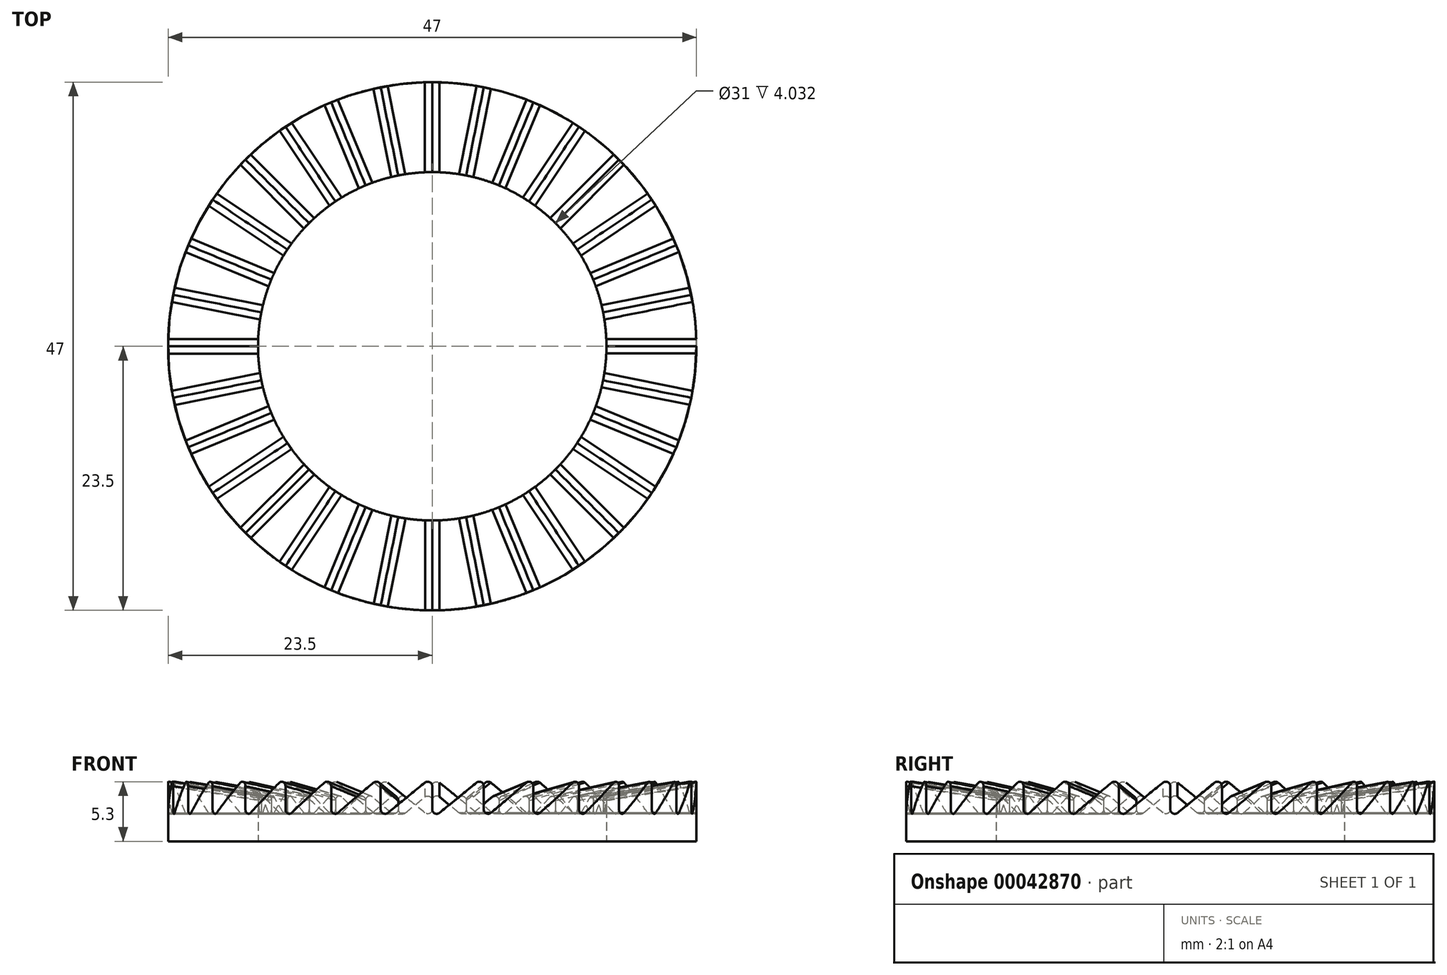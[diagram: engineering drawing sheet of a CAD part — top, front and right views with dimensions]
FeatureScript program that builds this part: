
annotation { "Feature Type Name" : "Feature", "Feature Type Description" : "" }
export const myFeature = defineFeature(function(context is Context, id is Id, definition is map)
    precondition{}
    {
        {
            var Q0;
            Q0=qCreatedBy(makeId("Top.planeOp"),FACE);
            var sketch = newSketch(context, id + "F0", { "sketchPlane" : qUnion([Q0])});
            skCircle(sketch, "E0", {"center": v(0, 0) * mm, "radius": 24 * mm});
            skCircle(sketch, "E1", {"center": v(0, 0) * mm, "radius": 25 * mm});
            skCircle(sketch, "E2", {"center": v(0, 0) * mm, "radius": 13 * mm});
            skCircle(sketch, "E3", {"center": v(0, 0) * mm, "radius": 15.5 * mm});
            skCircle(sketch, "E4", {"center": v(0, 0) * mm, "radius": 23.5 * mm});
            skCircle(sketch, "E5", {"center": v(0, 0) * mm, "radius": 12.5 * mm});
            skSolve(sketch);
        }
        {
            var Q0;
            Q0=makeQuery(id+"F0.imprint","IMPRINT",FACE,{"disambiguationData":[TD([[makeQuery(id+"F0.imprint","IMPRINT",EDGE,{"derivedFrom":sQuery(id+"F0.wireOp",EDGE,"E3")}),-1.0]])]});
            extrude(context, id + "F1", {"entities" : qUnion([Q0]), "depth" : 10 * mm});
        }
        {
            var Q0;
            Q0=qCreatedBy(makeId("Right.planeOp"),FACE);
            var sketch = newSketch(context, id + "F2", { "sketchPlane" : qUnion([Q0])});
            skLineSegment(sketch, "E6", {"start": v(0, 10) * mm, "end": v(0, 2) * mm});
            skLineSegment(sketch, "E7", {"start": v(0, 2) * mm, "end": v(9.8, 10) * mm});
            skLineSegment(sketch, "E8", {"start": v(0, 10) * mm, "end": v(9.8, 10) * mm});
            skSolve(sketch);
        }
        {
            var Q0;
            Q0=makeQuery(id+"F2.imprint","IMPRINT",FACE,{"disambiguationData":[TD([[makeQuery(id+"F2.imprint","IMPRINT",EDGE,{"derivedFrom":sQuery(id+"F2.wireOp",EDGE,"E6")}),1.0]])]});
            extrude(context, id + "F3", {"entities" : qUnion([Q0]), "depth" : 23.5 * mm});
        }
        {
            var Q0;
            Q0=makeQuery(id+"F3.opExtrude","SWEPT_BODY",BODY,{"disambiguationData":[OSD([sQuery(id+"F2.wireOp",EDGE,"E6"),sQuery(id+"F2.wireOp",EDGE,"E7"),sQuery(id+"F2.wireOp",EDGE,"E8")])]});
            var Q1;
            Q1=makeQuery(id+"F3.opExtrude","CAP_EDGE",EDGE,{"disambiguationData":[OSD([sQuery(id+"F2.wireOp",EDGE,"E6")])],"isStart":true});
            circularPattern(context, id + "F4", {"entities" : qUnion([Q0]), "axis" : qUnion([Q1]), "angle" : 11.25 * degree, "instanceCount" : 32});
        }
        {
            var Q0;
            Q0=makeQuery(id+"F3.opExtrude","SWEPT_BODY",BODY,{"disambiguationData":[OSD([sQuery(id+"F2.wireOp",EDGE,"E6"),sQuery(id+"F2.wireOp",EDGE,"E7"),sQuery(id+"F2.wireOp",EDGE,"E8")])]});
            var Q1;
            Q1=makeQuery(id+"F4.opPattern","COPY",BODY,{"derivedFrom":makeQuery(id+"F3.opExtrude","SWEPT_BODY",BODY,{"disambiguationData":[OSD([sQuery(id+"F2.wireOp",EDGE,"E6"),sQuery(id+"F2.wireOp",EDGE,"E7"),sQuery(id+"F2.wireOp",EDGE,"E8")])]}),"instanceName":"1"});
            var Q2;
            Q2=makeQuery(id+"F4.opPattern","COPY",BODY,{"derivedFrom":makeQuery(id+"F3.opExtrude","SWEPT_BODY",BODY,{"disambiguationData":[OSD([sQuery(id+"F2.wireOp",EDGE,"E6"),sQuery(id+"F2.wireOp",EDGE,"E7"),sQuery(id+"F2.wireOp",EDGE,"E8")])]}),"instanceName":"2"});
            var Q3;
            Q3=makeQuery(id+"F4.opPattern","COPY",BODY,{"derivedFrom":makeQuery(id+"F3.opExtrude","SWEPT_BODY",BODY,{"disambiguationData":[OSD([sQuery(id+"F2.wireOp",EDGE,"E6"),sQuery(id+"F2.wireOp",EDGE,"E7"),sQuery(id+"F2.wireOp",EDGE,"E8")])]}),"instanceName":"3"});
            var Q4;
            Q4=makeQuery(id+"F4.opPattern","COPY",BODY,{"derivedFrom":makeQuery(id+"F3.opExtrude","SWEPT_BODY",BODY,{"disambiguationData":[OSD([sQuery(id+"F2.wireOp",EDGE,"E6"),sQuery(id+"F2.wireOp",EDGE,"E7"),sQuery(id+"F2.wireOp",EDGE,"E8")])]}),"instanceName":"4"});
            var Q5;
            Q5=makeQuery(id+"F4.opPattern","COPY",BODY,{"derivedFrom":makeQuery(id+"F3.opExtrude","SWEPT_BODY",BODY,{"disambiguationData":[OSD([sQuery(id+"F2.wireOp",EDGE,"E6"),sQuery(id+"F2.wireOp",EDGE,"E7"),sQuery(id+"F2.wireOp",EDGE,"E8")])]}),"instanceName":"5"});
            var Q6;
            Q6=makeQuery(id+"F4.opPattern","COPY",BODY,{"derivedFrom":makeQuery(id+"F3.opExtrude","SWEPT_BODY",BODY,{"disambiguationData":[OSD([sQuery(id+"F2.wireOp",EDGE,"E6"),sQuery(id+"F2.wireOp",EDGE,"E7"),sQuery(id+"F2.wireOp",EDGE,"E8")])]}),"instanceName":"6"});
            var Q7;
            Q7=makeQuery(id+"F4.opPattern","COPY",BODY,{"derivedFrom":makeQuery(id+"F3.opExtrude","SWEPT_BODY",BODY,{"disambiguationData":[OSD([sQuery(id+"F2.wireOp",EDGE,"E6"),sQuery(id+"F2.wireOp",EDGE,"E7"),sQuery(id+"F2.wireOp",EDGE,"E8")])]}),"instanceName":"7"});
            var Q8;
            Q8=makeQuery(id+"F4.opPattern","COPY",BODY,{"derivedFrom":makeQuery(id+"F3.opExtrude","SWEPT_BODY",BODY,{"disambiguationData":[OSD([sQuery(id+"F2.wireOp",EDGE,"E6"),sQuery(id+"F2.wireOp",EDGE,"E7"),sQuery(id+"F2.wireOp",EDGE,"E8")])]}),"instanceName":"8"});
            var Q9;
            Q9=makeQuery(id+"F4.opPattern","COPY",BODY,{"derivedFrom":makeQuery(id+"F3.opExtrude","SWEPT_BODY",BODY,{"disambiguationData":[OSD([sQuery(id+"F2.wireOp",EDGE,"E6"),sQuery(id+"F2.wireOp",EDGE,"E7"),sQuery(id+"F2.wireOp",EDGE,"E8")])]}),"instanceName":"9"});
            var Q10;
            Q10=makeQuery(id+"F4.opPattern","COPY",BODY,{"derivedFrom":makeQuery(id+"F3.opExtrude","SWEPT_BODY",BODY,{"disambiguationData":[OSD([sQuery(id+"F2.wireOp",EDGE,"E6"),sQuery(id+"F2.wireOp",EDGE,"E7"),sQuery(id+"F2.wireOp",EDGE,"E8")])]}),"instanceName":"10"});
            var Q11;
            Q11=makeQuery(id+"F4.opPattern","COPY",BODY,{"derivedFrom":makeQuery(id+"F3.opExtrude","SWEPT_BODY",BODY,{"disambiguationData":[OSD([sQuery(id+"F2.wireOp",EDGE,"E6"),sQuery(id+"F2.wireOp",EDGE,"E7"),sQuery(id+"F2.wireOp",EDGE,"E8")])]}),"instanceName":"11"});
            var Q12;
            Q12=makeQuery(id+"F4.opPattern","COPY",BODY,{"derivedFrom":makeQuery(id+"F3.opExtrude","SWEPT_BODY",BODY,{"disambiguationData":[OSD([sQuery(id+"F2.wireOp",EDGE,"E6"),sQuery(id+"F2.wireOp",EDGE,"E7"),sQuery(id+"F2.wireOp",EDGE,"E8")])]}),"instanceName":"12"});
            var Q13;
            Q13=makeQuery(id+"F4.opPattern","COPY",BODY,{"derivedFrom":makeQuery(id+"F3.opExtrude","SWEPT_BODY",BODY,{"disambiguationData":[OSD([sQuery(id+"F2.wireOp",EDGE,"E6"),sQuery(id+"F2.wireOp",EDGE,"E7"),sQuery(id+"F2.wireOp",EDGE,"E8")])]}),"instanceName":"13"});
            var Q14;
            Q14=makeQuery(id+"F4.opPattern","COPY",BODY,{"derivedFrom":makeQuery(id+"F3.opExtrude","SWEPT_BODY",BODY,{"disambiguationData":[OSD([sQuery(id+"F2.wireOp",EDGE,"E6"),sQuery(id+"F2.wireOp",EDGE,"E7"),sQuery(id+"F2.wireOp",EDGE,"E8")])]}),"instanceName":"14"});
            var Q15;
            Q15=makeQuery(id+"F4.opPattern","COPY",BODY,{"derivedFrom":makeQuery(id+"F3.opExtrude","SWEPT_BODY",BODY,{"disambiguationData":[OSD([sQuery(id+"F2.wireOp",EDGE,"E6"),sQuery(id+"F2.wireOp",EDGE,"E7"),sQuery(id+"F2.wireOp",EDGE,"E8")])]}),"instanceName":"15"});
            var Q16;
            Q16=makeQuery(id+"F4.opPattern","COPY",BODY,{"derivedFrom":makeQuery(id+"F3.opExtrude","SWEPT_BODY",BODY,{"disambiguationData":[OSD([sQuery(id+"F2.wireOp",EDGE,"E6"),sQuery(id+"F2.wireOp",EDGE,"E7"),sQuery(id+"F2.wireOp",EDGE,"E8")])]}),"instanceName":"16"});
            var Q17;
            Q17=makeQuery(id+"F4.opPattern","COPY",BODY,{"derivedFrom":makeQuery(id+"F3.opExtrude","SWEPT_BODY",BODY,{"disambiguationData":[OSD([sQuery(id+"F2.wireOp",EDGE,"E6"),sQuery(id+"F2.wireOp",EDGE,"E7"),sQuery(id+"F2.wireOp",EDGE,"E8")])]}),"instanceName":"17"});
            var Q18;
            Q18=makeQuery(id+"F4.opPattern","COPY",BODY,{"derivedFrom":makeQuery(id+"F3.opExtrude","SWEPT_BODY",BODY,{"disambiguationData":[OSD([sQuery(id+"F2.wireOp",EDGE,"E6"),sQuery(id+"F2.wireOp",EDGE,"E7"),sQuery(id+"F2.wireOp",EDGE,"E8")])]}),"instanceName":"18"});
            var Q19;
            Q19=makeQuery(id+"F4.opPattern","COPY",BODY,{"derivedFrom":makeQuery(id+"F3.opExtrude","SWEPT_BODY",BODY,{"disambiguationData":[OSD([sQuery(id+"F2.wireOp",EDGE,"E6"),sQuery(id+"F2.wireOp",EDGE,"E7"),sQuery(id+"F2.wireOp",EDGE,"E8")])]}),"instanceName":"19"});
            var Q20;
            Q20=makeQuery(id+"F4.opPattern","COPY",BODY,{"derivedFrom":makeQuery(id+"F3.opExtrude","SWEPT_BODY",BODY,{"disambiguationData":[OSD([sQuery(id+"F2.wireOp",EDGE,"E6"),sQuery(id+"F2.wireOp",EDGE,"E7"),sQuery(id+"F2.wireOp",EDGE,"E8")])]}),"instanceName":"20"});
            var Q21;
            Q21=makeQuery(id+"F4.opPattern","COPY",BODY,{"derivedFrom":makeQuery(id+"F3.opExtrude","SWEPT_BODY",BODY,{"disambiguationData":[OSD([sQuery(id+"F2.wireOp",EDGE,"E6"),sQuery(id+"F2.wireOp",EDGE,"E7"),sQuery(id+"F2.wireOp",EDGE,"E8")])]}),"instanceName":"21"});
            var Q22;
            Q22=makeQuery(id+"F4.opPattern","COPY",BODY,{"derivedFrom":makeQuery(id+"F3.opExtrude","SWEPT_BODY",BODY,{"disambiguationData":[OSD([sQuery(id+"F2.wireOp",EDGE,"E6"),sQuery(id+"F2.wireOp",EDGE,"E7"),sQuery(id+"F2.wireOp",EDGE,"E8")])]}),"instanceName":"22"});
            var Q23;
            Q23=makeQuery(id+"F4.opPattern","COPY",BODY,{"derivedFrom":makeQuery(id+"F3.opExtrude","SWEPT_BODY",BODY,{"disambiguationData":[OSD([sQuery(id+"F2.wireOp",EDGE,"E6"),sQuery(id+"F2.wireOp",EDGE,"E7"),sQuery(id+"F2.wireOp",EDGE,"E8")])]}),"instanceName":"23"});
            var Q24;
            Q24=makeQuery(id+"F4.opPattern","COPY",BODY,{"derivedFrom":makeQuery(id+"F3.opExtrude","SWEPT_BODY",BODY,{"disambiguationData":[OSD([sQuery(id+"F2.wireOp",EDGE,"E6"),sQuery(id+"F2.wireOp",EDGE,"E7"),sQuery(id+"F2.wireOp",EDGE,"E8")])]}),"instanceName":"24"});
            var Q25;
            Q25=makeQuery(id+"F4.opPattern","COPY",BODY,{"derivedFrom":makeQuery(id+"F3.opExtrude","SWEPT_BODY",BODY,{"disambiguationData":[OSD([sQuery(id+"F2.wireOp",EDGE,"E6"),sQuery(id+"F2.wireOp",EDGE,"E7"),sQuery(id+"F2.wireOp",EDGE,"E8")])]}),"instanceName":"25"});
            var Q26;
            Q26=makeQuery(id+"F4.opPattern","COPY",BODY,{"derivedFrom":makeQuery(id+"F3.opExtrude","SWEPT_BODY",BODY,{"disambiguationData":[OSD([sQuery(id+"F2.wireOp",EDGE,"E6"),sQuery(id+"F2.wireOp",EDGE,"E7"),sQuery(id+"F2.wireOp",EDGE,"E8")])]}),"instanceName":"26"});
            var Q27;
            Q27=makeQuery(id+"F4.opPattern","COPY",BODY,{"derivedFrom":makeQuery(id+"F3.opExtrude","SWEPT_BODY",BODY,{"disambiguationData":[OSD([sQuery(id+"F2.wireOp",EDGE,"E6"),sQuery(id+"F2.wireOp",EDGE,"E7"),sQuery(id+"F2.wireOp",EDGE,"E8")])]}),"instanceName":"27"});
            var Q28;
            Q28=makeQuery(id+"F4.opPattern","COPY",BODY,{"derivedFrom":makeQuery(id+"F3.opExtrude","SWEPT_BODY",BODY,{"disambiguationData":[OSD([sQuery(id+"F2.wireOp",EDGE,"E6"),sQuery(id+"F2.wireOp",EDGE,"E7"),sQuery(id+"F2.wireOp",EDGE,"E8")])]}),"instanceName":"28"});
            var Q29;
            Q29=makeQuery(id+"F4.opPattern","COPY",BODY,{"derivedFrom":makeQuery(id+"F3.opExtrude","SWEPT_BODY",BODY,{"disambiguationData":[OSD([sQuery(id+"F2.wireOp",EDGE,"E6"),sQuery(id+"F2.wireOp",EDGE,"E7"),sQuery(id+"F2.wireOp",EDGE,"E8")])]}),"instanceName":"29"});
            var Q30;
            Q30=makeQuery(id+"F4.opPattern","COPY",BODY,{"derivedFrom":makeQuery(id+"F3.opExtrude","SWEPT_BODY",BODY,{"disambiguationData":[OSD([sQuery(id+"F2.wireOp",EDGE,"E6"),sQuery(id+"F2.wireOp",EDGE,"E7"),sQuery(id+"F2.wireOp",EDGE,"E8")])]}),"instanceName":"30"});
            var Q31;
            Q31=makeQuery(id+"F4.opPattern","COPY",BODY,{"derivedFrom":makeQuery(id+"F3.opExtrude","SWEPT_BODY",BODY,{"disambiguationData":[OSD([sQuery(id+"F2.wireOp",EDGE,"E6"),sQuery(id+"F2.wireOp",EDGE,"E7"),sQuery(id+"F2.wireOp",EDGE,"E8")])]}),"instanceName":"31"});
            booleanBodies(context, id + "F5", {"operationType" : BooleanOperationType.UNION, "tools" : qUnion([Q0, Q1, Q2, Q3, Q4, Q5, Q6, Q7, Q8, Q9, Q10, Q11, Q12, Q13, Q14, Q15, Q16, Q17, Q18, Q19, Q20, Q21, Q22, Q23, Q24, Q25, Q26, Q27, Q28, Q29, Q30, Q31])});
        }
        {
            var Q0;
            Q0=makeQuery(id+"F3.opExtrude","SWEPT_BODY",BODY,{"disambiguationData":[OSD([sQuery(id+"F2.wireOp",EDGE,"E6"),sQuery(id+"F2.wireOp",EDGE,"E7"),sQuery(id+"F2.wireOp",EDGE,"E8")])]});
            var Q1;
            Q1=makeQuery(id+"F1.opExtrude","SWEPT_BODY",BODY,{"disambiguationData":[OSD([sQuery(id+"F0.wireOp",EDGE,"E3"),sQuery(id+"F0.wireOp",EDGE,"E4")])]});
            booleanBodies(context, id + "F6", {"operationType" : BooleanOperationType.SUBTRACTION, "tools" : qUnion([Q0]), "targets" : qUnion([Q1])});
        }
        {
            var Q0;
            Q0=makeQuery(id+"F6.opBoolean","COPY",EDGE,{"derivedFrom":makeQuery(id+"F4.opPattern","COPY",EDGE,{"derivedFrom":makeQuery(id+"F3.opExtrude","SWEPT_EDGE",EDGE,{"disambiguationData":[OSD([sQuery(id+"F2.wireOp",EDGE,"E6"),sQuery(id+"F2.wireOp",EDGE,"E7")])]}),"instanceName":"6"})});
            var Q1;
            Q1=makeQuery(id+"F6.opBoolean","COPY",EDGE,{"derivedFrom":makeQuery(id+"F5.opBoolean","INTERSECT",EDGE,{"derivedFrom":[makeQuery(id+"F4.opPattern","COPY",FACE,{"derivedFrom":makeQuery(id+"F3.opExtrude","SWEPT_FACE",FACE,{"disambiguationData":[OSD([sQuery(id+"F2.wireOp",EDGE,"E6")])]}),"instanceName":"5"}),makeQuery(id+"F4.opPattern","COPY",FACE,{"derivedFrom":makeQuery(id+"F3.opExtrude","SWEPT_FACE",FACE,{"disambiguationData":[OSD([sQuery(id+"F2.wireOp",EDGE,"E7")])]}),"instanceName":"6"})]})});
            var Q2;
            Q2=makeQuery(id+"F6.opBoolean","COPY",EDGE,{"derivedFrom":makeQuery(id+"F4.opPattern","COPY",EDGE,{"derivedFrom":makeQuery(id+"F3.opExtrude","SWEPT_EDGE",EDGE,{"disambiguationData":[OSD([sQuery(id+"F2.wireOp",EDGE,"E6"),sQuery(id+"F2.wireOp",EDGE,"E7")])]}),"instanceName":"5"})});
            var Q3;
            Q3=makeQuery(id+"F6.opBoolean","COPY",EDGE,{"derivedFrom":makeQuery(id+"F5.opBoolean","INTERSECT",EDGE,{"derivedFrom":[makeQuery(id+"F4.opPattern","COPY",FACE,{"derivedFrom":makeQuery(id+"F3.opExtrude","SWEPT_FACE",FACE,{"disambiguationData":[OSD([sQuery(id+"F2.wireOp",EDGE,"E6")])]}),"instanceName":"4"}),makeQuery(id+"F4.opPattern","COPY",FACE,{"derivedFrom":makeQuery(id+"F3.opExtrude","SWEPT_FACE",FACE,{"disambiguationData":[OSD([sQuery(id+"F2.wireOp",EDGE,"E7")])]}),"instanceName":"5"})]})});
            var Q4;
            Q4=makeQuery(id+"F6.opBoolean","COPY",EDGE,{"derivedFrom":makeQuery(id+"F4.opPattern","COPY",EDGE,{"derivedFrom":makeQuery(id+"F3.opExtrude","SWEPT_EDGE",EDGE,{"disambiguationData":[OSD([sQuery(id+"F2.wireOp",EDGE,"E6"),sQuery(id+"F2.wireOp",EDGE,"E7")])]}),"instanceName":"4"})});
            var Q5;
            Q5=makeQuery(id+"F6.opBoolean","COPY",EDGE,{"derivedFrom":makeQuery(id+"F5.opBoolean","INTERSECT",EDGE,{"derivedFrom":[makeQuery(id+"F4.opPattern","COPY",FACE,{"derivedFrom":makeQuery(id+"F3.opExtrude","SWEPT_FACE",FACE,{"disambiguationData":[OSD([sQuery(id+"F2.wireOp",EDGE,"E6")])]}),"instanceName":"3"}),makeQuery(id+"F4.opPattern","COPY",FACE,{"derivedFrom":makeQuery(id+"F3.opExtrude","SWEPT_FACE",FACE,{"disambiguationData":[OSD([sQuery(id+"F2.wireOp",EDGE,"E7")])]}),"instanceName":"4"})]})});
            var Q6;
            Q6=makeQuery(id+"F6.opBoolean","COPY",EDGE,{"derivedFrom":makeQuery(id+"F4.opPattern","COPY",EDGE,{"derivedFrom":makeQuery(id+"F3.opExtrude","SWEPT_EDGE",EDGE,{"disambiguationData":[OSD([sQuery(id+"F2.wireOp",EDGE,"E6"),sQuery(id+"F2.wireOp",EDGE,"E7")])]}),"instanceName":"3"})});
            var Q7;
            Q7=makeQuery(id+"F6.opBoolean","COPY",EDGE,{"derivedFrom":makeQuery(id+"F5.opBoolean","INTERSECT",EDGE,{"derivedFrom":[makeQuery(id+"F4.opPattern","COPY",FACE,{"derivedFrom":makeQuery(id+"F3.opExtrude","SWEPT_FACE",FACE,{"disambiguationData":[OSD([sQuery(id+"F2.wireOp",EDGE,"E6")])]}),"instanceName":"2"}),makeQuery(id+"F4.opPattern","COPY",FACE,{"derivedFrom":makeQuery(id+"F3.opExtrude","SWEPT_FACE",FACE,{"disambiguationData":[OSD([sQuery(id+"F2.wireOp",EDGE,"E7")])]}),"instanceName":"3"})]})});
            var Q8;
            Q8=makeQuery(id+"F6.opBoolean","COPY",EDGE,{"derivedFrom":makeQuery(id+"F4.opPattern","COPY",EDGE,{"derivedFrom":makeQuery(id+"F3.opExtrude","SWEPT_EDGE",EDGE,{"disambiguationData":[OSD([sQuery(id+"F2.wireOp",EDGE,"E6"),sQuery(id+"F2.wireOp",EDGE,"E7")])]}),"instanceName":"2"})});
            var Q9;
            Q9=makeQuery(id+"F6.opBoolean","COPY",EDGE,{"derivedFrom":makeQuery(id+"F5.opBoolean","INTERSECT",EDGE,{"derivedFrom":[makeQuery(id+"F4.opPattern","COPY",FACE,{"derivedFrom":makeQuery(id+"F3.opExtrude","SWEPT_FACE",FACE,{"disambiguationData":[OSD([sQuery(id+"F2.wireOp",EDGE,"E6")])]}),"instanceName":"1"}),makeQuery(id+"F4.opPattern","COPY",FACE,{"derivedFrom":makeQuery(id+"F3.opExtrude","SWEPT_FACE",FACE,{"disambiguationData":[OSD([sQuery(id+"F2.wireOp",EDGE,"E7")])]}),"instanceName":"2"})]})});
            var Q10;
            Q10=makeQuery(id+"F6.opBoolean","COPY",EDGE,{"derivedFrom":makeQuery(id+"F4.opPattern","COPY",EDGE,{"derivedFrom":makeQuery(id+"F3.opExtrude","SWEPT_EDGE",EDGE,{"disambiguationData":[OSD([sQuery(id+"F2.wireOp",EDGE,"E6"),sQuery(id+"F2.wireOp",EDGE,"E7")])]}),"instanceName":"1"})});
            var Q11;
            Q11=makeQuery(id+"F6.opBoolean","COPY",EDGE,{"derivedFrom":makeQuery(id+"F3.opExtrude","SWEPT_EDGE",EDGE,{"disambiguationData":[OSD([sQuery(id+"F2.wireOp",EDGE,"E6"),sQuery(id+"F2.wireOp",EDGE,"E7")])]})});
            var Q12;
            Q12=makeQuery(id+"F6.opBoolean","COPY",EDGE,{"derivedFrom":makeQuery(id+"F5.opBoolean","INTERSECT",EDGE,{"derivedFrom":[makeQuery(id+"F3.opExtrude","SWEPT_FACE",FACE,{"disambiguationData":[OSD([sQuery(id+"F2.wireOp",EDGE,"E6")])]}),makeQuery(id+"F4.opPattern","COPY",FACE,{"derivedFrom":makeQuery(id+"F3.opExtrude","SWEPT_FACE",FACE,{"disambiguationData":[OSD([sQuery(id+"F2.wireOp",EDGE,"E7")])]}),"instanceName":"1"})]})});
            var Q13;
            {var subQ0=sQuery(id+"F2.wireOp",EDGE,"E7");var subQ1=sQuery(id+"F2.wireOp",EDGE,"E6");Q13=makeQuery(id+"F6.opBoolean","COPY",EDGE,{"derivedFrom":makeQuery(id+"F5.opBoolean","INTERSECT",EDGE,{"derivedFrom":[makeQuery(id+"F3.opExtrude","SWEPT_FACE",FACE,{"disambiguationData":[OSD([subQ0])]}),makeQuery(id+"F4.opPattern","COPY",FACE,{"derivedFrom":makeQuery(id+"F3.opExtrude","CAP_FACE",FACE,{"disambiguationData":[OSD([subQ1,subQ0,sQuery(id+"F2.wireOp",EDGE,"E8")])],"isStart":true}),"instanceName":"23"}),makeQuery(id+"F4.opPattern","COPY",FACE,{"derivedFrom":makeQuery(id+"F3.opExtrude","SWEPT_FACE",FACE,{"disambiguationData":[OSD([subQ1])]}),"instanceName":"31"})]})});}
            var Q14;
            Q14=makeQuery(id+"F6.opBoolean","COPY",EDGE,{"derivedFrom":makeQuery(id+"F4.opPattern","COPY",EDGE,{"derivedFrom":makeQuery(id+"F3.opExtrude","SWEPT_EDGE",EDGE,{"disambiguationData":[OSD([sQuery(id+"F2.wireOp",EDGE,"E6"),sQuery(id+"F2.wireOp",EDGE,"E7")])]}),"instanceName":"31"})});
            var Q15;
            Q15=makeQuery(id+"F6.opBoolean","COPY",EDGE,{"derivedFrom":makeQuery(id+"F5.opBoolean","INTERSECT",EDGE,{"derivedFrom":[makeQuery(id+"F4.opPattern","COPY",FACE,{"derivedFrom":makeQuery(id+"F3.opExtrude","SWEPT_FACE",FACE,{"disambiguationData":[OSD([sQuery(id+"F2.wireOp",EDGE,"E6")])]}),"instanceName":"30"}),makeQuery(id+"F4.opPattern","COPY",FACE,{"derivedFrom":makeQuery(id+"F3.opExtrude","SWEPT_FACE",FACE,{"disambiguationData":[OSD([sQuery(id+"F2.wireOp",EDGE,"E7")])]}),"instanceName":"31"})]})});
            var Q16;
            Q16=makeQuery(id+"F6.opBoolean","COPY",EDGE,{"derivedFrom":makeQuery(id+"F5.opBoolean","INTERSECT",EDGE,{"derivedFrom":[makeQuery(id+"F4.opPattern","COPY",FACE,{"derivedFrom":makeQuery(id+"F3.opExtrude","SWEPT_FACE",FACE,{"disambiguationData":[OSD([sQuery(id+"F2.wireOp",EDGE,"E6")])]}),"instanceName":"29"}),makeQuery(id+"F4.opPattern","COPY",FACE,{"derivedFrom":makeQuery(id+"F3.opExtrude","SWEPT_FACE",FACE,{"disambiguationData":[OSD([sQuery(id+"F2.wireOp",EDGE,"E7")])]}),"instanceName":"30"})]})});
            var Q17;
            Q17=makeQuery(id+"F6.opBoolean","COPY",EDGE,{"derivedFrom":makeQuery(id+"F4.opPattern","COPY",EDGE,{"derivedFrom":makeQuery(id+"F3.opExtrude","SWEPT_EDGE",EDGE,{"disambiguationData":[OSD([sQuery(id+"F2.wireOp",EDGE,"E6"),sQuery(id+"F2.wireOp",EDGE,"E7")])]}),"instanceName":"29"})});
            var Q18;
            Q18=makeQuery(id+"F6.opBoolean","COPY",EDGE,{"derivedFrom":makeQuery(id+"F4.opPattern","COPY",EDGE,{"derivedFrom":makeQuery(id+"F3.opExtrude","SWEPT_EDGE",EDGE,{"disambiguationData":[OSD([sQuery(id+"F2.wireOp",EDGE,"E6"),sQuery(id+"F2.wireOp",EDGE,"E7")])]}),"instanceName":"30"})});
            var Q19;
            Q19=makeQuery(id+"F6.opBoolean","COPY",EDGE,{"derivedFrom":makeQuery(id+"F5.opBoolean","INTERSECT",EDGE,{"derivedFrom":[makeQuery(id+"F4.opPattern","COPY",FACE,{"derivedFrom":makeQuery(id+"F3.opExtrude","SWEPT_FACE",FACE,{"disambiguationData":[OSD([sQuery(id+"F2.wireOp",EDGE,"E6")])]}),"instanceName":"28"}),makeQuery(id+"F4.opPattern","COPY",FACE,{"derivedFrom":makeQuery(id+"F3.opExtrude","SWEPT_FACE",FACE,{"disambiguationData":[OSD([sQuery(id+"F2.wireOp",EDGE,"E7")])]}),"instanceName":"29"})]})});
            var Q20;
            Q20=makeQuery(id+"F6.opBoolean","COPY",EDGE,{"derivedFrom":makeQuery(id+"F4.opPattern","COPY",EDGE,{"derivedFrom":makeQuery(id+"F3.opExtrude","SWEPT_EDGE",EDGE,{"disambiguationData":[OSD([sQuery(id+"F2.wireOp",EDGE,"E6"),sQuery(id+"F2.wireOp",EDGE,"E7")])]}),"instanceName":"28"})});
            var Q21;
            Q21=makeQuery(id+"F6.opBoolean","COPY",EDGE,{"derivedFrom":makeQuery(id+"F5.opBoolean","INTERSECT",EDGE,{"derivedFrom":[makeQuery(id+"F4.opPattern","COPY",FACE,{"derivedFrom":makeQuery(id+"F3.opExtrude","SWEPT_FACE",FACE,{"disambiguationData":[OSD([sQuery(id+"F2.wireOp",EDGE,"E6")])]}),"instanceName":"27"}),makeQuery(id+"F4.opPattern","COPY",FACE,{"derivedFrom":makeQuery(id+"F3.opExtrude","SWEPT_FACE",FACE,{"disambiguationData":[OSD([sQuery(id+"F2.wireOp",EDGE,"E7")])]}),"instanceName":"28"})]})});
            var Q22;
            Q22=makeQuery(id+"F6.opBoolean","COPY",EDGE,{"derivedFrom":makeQuery(id+"F4.opPattern","COPY",EDGE,{"derivedFrom":makeQuery(id+"F3.opExtrude","SWEPT_EDGE",EDGE,{"disambiguationData":[OSD([sQuery(id+"F2.wireOp",EDGE,"E6"),sQuery(id+"F2.wireOp",EDGE,"E7")])]}),"instanceName":"27"})});
            var Q23;
            Q23=makeQuery(id+"F6.opBoolean","COPY",EDGE,{"derivedFrom":makeQuery(id+"F5.opBoolean","INTERSECT",EDGE,{"derivedFrom":[makeQuery(id+"F4.opPattern","COPY",FACE,{"derivedFrom":makeQuery(id+"F3.opExtrude","SWEPT_FACE",FACE,{"disambiguationData":[OSD([sQuery(id+"F2.wireOp",EDGE,"E6")])]}),"instanceName":"26"}),makeQuery(id+"F4.opPattern","COPY",FACE,{"derivedFrom":makeQuery(id+"F3.opExtrude","SWEPT_FACE",FACE,{"disambiguationData":[OSD([sQuery(id+"F2.wireOp",EDGE,"E7")])]}),"instanceName":"27"})]})});
            var Q24;
            Q24=makeQuery(id+"F6.opBoolean","COPY",EDGE,{"derivedFrom":makeQuery(id+"F4.opPattern","COPY",EDGE,{"derivedFrom":makeQuery(id+"F3.opExtrude","SWEPT_EDGE",EDGE,{"disambiguationData":[OSD([sQuery(id+"F2.wireOp",EDGE,"E6"),sQuery(id+"F2.wireOp",EDGE,"E7")])]}),"instanceName":"26"})});
            var Q25;
            Q25=makeQuery(id+"F6.opBoolean","COPY",EDGE,{"derivedFrom":makeQuery(id+"F5.opBoolean","INTERSECT",EDGE,{"derivedFrom":[makeQuery(id+"F4.opPattern","COPY",FACE,{"derivedFrom":makeQuery(id+"F3.opExtrude","SWEPT_FACE",FACE,{"disambiguationData":[OSD([sQuery(id+"F2.wireOp",EDGE,"E6")])]}),"instanceName":"25"}),makeQuery(id+"F4.opPattern","COPY",FACE,{"derivedFrom":makeQuery(id+"F3.opExtrude","SWEPT_FACE",FACE,{"disambiguationData":[OSD([sQuery(id+"F2.wireOp",EDGE,"E7")])]}),"instanceName":"26"})]})});
            var Q26;
            Q26=makeQuery(id+"F6.opBoolean","COPY",EDGE,{"derivedFrom":makeQuery(id+"F4.opPattern","COPY",EDGE,{"derivedFrom":makeQuery(id+"F3.opExtrude","SWEPT_EDGE",EDGE,{"disambiguationData":[OSD([sQuery(id+"F2.wireOp",EDGE,"E6"),sQuery(id+"F2.wireOp",EDGE,"E7")])]}),"instanceName":"25"})});
            var Q27;
            Q27=makeQuery(id+"F6.opBoolean","COPY",EDGE,{"derivedFrom":makeQuery(id+"F5.opBoolean","INTERSECT",EDGE,{"derivedFrom":[makeQuery(id+"F4.opPattern","COPY",FACE,{"derivedFrom":makeQuery(id+"F3.opExtrude","SWEPT_FACE",FACE,{"disambiguationData":[OSD([sQuery(id+"F2.wireOp",EDGE,"E6")])]}),"instanceName":"24"}),makeQuery(id+"F4.opPattern","COPY",FACE,{"derivedFrom":makeQuery(id+"F3.opExtrude","SWEPT_FACE",FACE,{"disambiguationData":[OSD([sQuery(id+"F2.wireOp",EDGE,"E7")])]}),"instanceName":"25"})]})});
            var Q28;
            Q28=makeQuery(id+"F6.opBoolean","COPY",EDGE,{"derivedFrom":makeQuery(id+"F4.opPattern","COPY",EDGE,{"derivedFrom":makeQuery(id+"F3.opExtrude","SWEPT_EDGE",EDGE,{"disambiguationData":[OSD([sQuery(id+"F2.wireOp",EDGE,"E6"),sQuery(id+"F2.wireOp",EDGE,"E7")])]}),"instanceName":"24"})});
            var Q29;
            Q29=makeQuery(id+"F6.opBoolean","COPY",EDGE,{"derivedFrom":makeQuery(id+"F5.opBoolean","INTERSECT",EDGE,{"derivedFrom":[makeQuery(id+"F4.opPattern","COPY",FACE,{"derivedFrom":makeQuery(id+"F3.opExtrude","SWEPT_FACE",FACE,{"disambiguationData":[OSD([sQuery(id+"F2.wireOp",EDGE,"E6")])]}),"instanceName":"23"}),makeQuery(id+"F4.opPattern","COPY",FACE,{"derivedFrom":makeQuery(id+"F3.opExtrude","SWEPT_FACE",FACE,{"disambiguationData":[OSD([sQuery(id+"F2.wireOp",EDGE,"E7")])]}),"instanceName":"24"})]})});
            var Q30;
            Q30=makeQuery(id+"F6.opBoolean","COPY",EDGE,{"derivedFrom":makeQuery(id+"F4.opPattern","COPY",EDGE,{"derivedFrom":makeQuery(id+"F3.opExtrude","SWEPT_EDGE",EDGE,{"disambiguationData":[OSD([sQuery(id+"F2.wireOp",EDGE,"E6"),sQuery(id+"F2.wireOp",EDGE,"E7")])]}),"instanceName":"23"})});
            var Q31;
            Q31=makeQuery(id+"F6.opBoolean","COPY",EDGE,{"derivedFrom":makeQuery(id+"F5.opBoolean","INTERSECT",EDGE,{"derivedFrom":[makeQuery(id+"F4.opPattern","COPY",FACE,{"derivedFrom":makeQuery(id+"F3.opExtrude","SWEPT_FACE",FACE,{"disambiguationData":[OSD([sQuery(id+"F2.wireOp",EDGE,"E6")])]}),"instanceName":"22"}),makeQuery(id+"F4.opPattern","COPY",FACE,{"derivedFrom":makeQuery(id+"F3.opExtrude","SWEPT_FACE",FACE,{"disambiguationData":[OSD([sQuery(id+"F2.wireOp",EDGE,"E7")])]}),"instanceName":"23"})]})});
            var Q32;
            Q32=makeQuery(id+"F6.opBoolean","COPY",EDGE,{"derivedFrom":makeQuery(id+"F4.opPattern","COPY",EDGE,{"derivedFrom":makeQuery(id+"F3.opExtrude","SWEPT_EDGE",EDGE,{"disambiguationData":[OSD([sQuery(id+"F2.wireOp",EDGE,"E6"),sQuery(id+"F2.wireOp",EDGE,"E7")])]}),"instanceName":"22"})});
            var Q33;
            Q33=makeQuery(id+"F6.opBoolean","COPY",EDGE,{"derivedFrom":makeQuery(id+"F5.opBoolean","INTERSECT",EDGE,{"derivedFrom":[makeQuery(id+"F4.opPattern","COPY",FACE,{"derivedFrom":makeQuery(id+"F3.opExtrude","SWEPT_FACE",FACE,{"disambiguationData":[OSD([sQuery(id+"F2.wireOp",EDGE,"E6")])]}),"instanceName":"21"}),makeQuery(id+"F4.opPattern","COPY",FACE,{"derivedFrom":makeQuery(id+"F3.opExtrude","SWEPT_FACE",FACE,{"disambiguationData":[OSD([sQuery(id+"F2.wireOp",EDGE,"E7")])]}),"instanceName":"22"})]})});
            var Q34;
            Q34=makeQuery(id+"F6.opBoolean","COPY",EDGE,{"derivedFrom":makeQuery(id+"F4.opPattern","COPY",EDGE,{"derivedFrom":makeQuery(id+"F3.opExtrude","SWEPT_EDGE",EDGE,{"disambiguationData":[OSD([sQuery(id+"F2.wireOp",EDGE,"E6"),sQuery(id+"F2.wireOp",EDGE,"E7")])]}),"instanceName":"21"})});
            var Q35;
            Q35=makeQuery(id+"F6.opBoolean","COPY",EDGE,{"derivedFrom":makeQuery(id+"F5.opBoolean","INTERSECT",EDGE,{"derivedFrom":[makeQuery(id+"F4.opPattern","COPY",FACE,{"derivedFrom":makeQuery(id+"F3.opExtrude","SWEPT_FACE",FACE,{"disambiguationData":[OSD([sQuery(id+"F2.wireOp",EDGE,"E6")])]}),"instanceName":"20"}),makeQuery(id+"F4.opPattern","COPY",FACE,{"derivedFrom":makeQuery(id+"F3.opExtrude","SWEPT_FACE",FACE,{"disambiguationData":[OSD([sQuery(id+"F2.wireOp",EDGE,"E7")])]}),"instanceName":"21"})]})});
            var Q36;
            Q36=makeQuery(id+"F6.opBoolean","COPY",EDGE,{"derivedFrom":makeQuery(id+"F4.opPattern","COPY",EDGE,{"derivedFrom":makeQuery(id+"F3.opExtrude","SWEPT_EDGE",EDGE,{"disambiguationData":[OSD([sQuery(id+"F2.wireOp",EDGE,"E6"),sQuery(id+"F2.wireOp",EDGE,"E7")])]}),"instanceName":"20"})});
            var Q37;
            Q37=makeQuery(id+"F6.opBoolean","COPY",EDGE,{"derivedFrom":makeQuery(id+"F5.opBoolean","INTERSECT",EDGE,{"derivedFrom":[makeQuery(id+"F4.opPattern","COPY",FACE,{"derivedFrom":makeQuery(id+"F3.opExtrude","SWEPT_FACE",FACE,{"disambiguationData":[OSD([sQuery(id+"F2.wireOp",EDGE,"E6")])]}),"instanceName":"19"}),makeQuery(id+"F4.opPattern","COPY",FACE,{"derivedFrom":makeQuery(id+"F3.opExtrude","SWEPT_FACE",FACE,{"disambiguationData":[OSD([sQuery(id+"F2.wireOp",EDGE,"E7")])]}),"instanceName":"20"})]})});
            var Q38;
            Q38=makeQuery(id+"F6.opBoolean","COPY",EDGE,{"derivedFrom":makeQuery(id+"F4.opPattern","COPY",EDGE,{"derivedFrom":makeQuery(id+"F3.opExtrude","SWEPT_EDGE",EDGE,{"disambiguationData":[OSD([sQuery(id+"F2.wireOp",EDGE,"E6"),sQuery(id+"F2.wireOp",EDGE,"E7")])]}),"instanceName":"19"})});
            var Q39;
            Q39=makeQuery(id+"F6.opBoolean","COPY",EDGE,{"derivedFrom":makeQuery(id+"F5.opBoolean","INTERSECT",EDGE,{"derivedFrom":[makeQuery(id+"F4.opPattern","COPY",FACE,{"derivedFrom":makeQuery(id+"F3.opExtrude","SWEPT_FACE",FACE,{"disambiguationData":[OSD([sQuery(id+"F2.wireOp",EDGE,"E6")])]}),"instanceName":"18"}),makeQuery(id+"F4.opPattern","COPY",FACE,{"derivedFrom":makeQuery(id+"F3.opExtrude","SWEPT_FACE",FACE,{"disambiguationData":[OSD([sQuery(id+"F2.wireOp",EDGE,"E7")])]}),"instanceName":"19"})]})});
            var Q40;
            Q40=makeQuery(id+"F6.opBoolean","COPY",EDGE,{"derivedFrom":makeQuery(id+"F4.opPattern","COPY",EDGE,{"derivedFrom":makeQuery(id+"F3.opExtrude","SWEPT_EDGE",EDGE,{"disambiguationData":[OSD([sQuery(id+"F2.wireOp",EDGE,"E6"),sQuery(id+"F2.wireOp",EDGE,"E7")])]}),"instanceName":"18"})});
            var Q41;
            Q41=makeQuery(id+"F6.opBoolean","COPY",EDGE,{"derivedFrom":makeQuery(id+"F5.opBoolean","INTERSECT",EDGE,{"derivedFrom":[makeQuery(id+"F4.opPattern","COPY",FACE,{"derivedFrom":makeQuery(id+"F3.opExtrude","SWEPT_FACE",FACE,{"disambiguationData":[OSD([sQuery(id+"F2.wireOp",EDGE,"E6")])]}),"instanceName":"17"}),makeQuery(id+"F4.opPattern","COPY",FACE,{"derivedFrom":makeQuery(id+"F3.opExtrude","SWEPT_FACE",FACE,{"disambiguationData":[OSD([sQuery(id+"F2.wireOp",EDGE,"E7")])]}),"instanceName":"18"})]})});
            var Q42;
            Q42=makeQuery(id+"F6.opBoolean","COPY",EDGE,{"derivedFrom":makeQuery(id+"F4.opPattern","COPY",EDGE,{"derivedFrom":makeQuery(id+"F3.opExtrude","SWEPT_EDGE",EDGE,{"disambiguationData":[OSD([sQuery(id+"F2.wireOp",EDGE,"E6"),sQuery(id+"F2.wireOp",EDGE,"E7")])]}),"instanceName":"17"})});
            var Q43;
            Q43=makeQuery(id+"F6.opBoolean","COPY",EDGE,{"derivedFrom":makeQuery(id+"F5.opBoolean","INTERSECT",EDGE,{"derivedFrom":[makeQuery(id+"F4.opPattern","COPY",FACE,{"derivedFrom":makeQuery(id+"F3.opExtrude","SWEPT_FACE",FACE,{"disambiguationData":[OSD([sQuery(id+"F2.wireOp",EDGE,"E6")])]}),"instanceName":"16"}),makeQuery(id+"F4.opPattern","COPY",FACE,{"derivedFrom":makeQuery(id+"F3.opExtrude","SWEPT_FACE",FACE,{"disambiguationData":[OSD([sQuery(id+"F2.wireOp",EDGE,"E7")])]}),"instanceName":"17"})]})});
            var Q44;
            Q44=makeQuery(id+"F6.opBoolean","COPY",EDGE,{"derivedFrom":makeQuery(id+"F4.opPattern","COPY",EDGE,{"derivedFrom":makeQuery(id+"F3.opExtrude","SWEPT_EDGE",EDGE,{"disambiguationData":[OSD([sQuery(id+"F2.wireOp",EDGE,"E6"),sQuery(id+"F2.wireOp",EDGE,"E7")])]}),"instanceName":"16"})});
            var Q45;
            Q45=makeQuery(id+"F6.opBoolean","COPY",EDGE,{"derivedFrom":makeQuery(id+"F5.opBoolean","INTERSECT",EDGE,{"derivedFrom":[makeQuery(id+"F4.opPattern","COPY",FACE,{"derivedFrom":makeQuery(id+"F3.opExtrude","SWEPT_FACE",FACE,{"disambiguationData":[OSD([sQuery(id+"F2.wireOp",EDGE,"E6")])]}),"instanceName":"15"}),makeQuery(id+"F4.opPattern","COPY",FACE,{"derivedFrom":makeQuery(id+"F3.opExtrude","SWEPT_FACE",FACE,{"disambiguationData":[OSD([sQuery(id+"F2.wireOp",EDGE,"E7")])]}),"instanceName":"16"})]})});
            var Q46;
            Q46=makeQuery(id+"F6.opBoolean","COPY",EDGE,{"derivedFrom":makeQuery(id+"F4.opPattern","COPY",EDGE,{"derivedFrom":makeQuery(id+"F3.opExtrude","SWEPT_EDGE",EDGE,{"disambiguationData":[OSD([sQuery(id+"F2.wireOp",EDGE,"E6"),sQuery(id+"F2.wireOp",EDGE,"E7")])]}),"instanceName":"15"})});
            var Q47;
            Q47=makeQuery(id+"F6.opBoolean","COPY",EDGE,{"derivedFrom":makeQuery(id+"F4.opPattern","COPY",EDGE,{"derivedFrom":makeQuery(id+"F3.opExtrude","SWEPT_EDGE",EDGE,{"disambiguationData":[OSD([sQuery(id+"F2.wireOp",EDGE,"E6"),sQuery(id+"F2.wireOp",EDGE,"E7")])]}),"instanceName":"14"})});
            var Q48;
            Q48=makeQuery(id+"F6.opBoolean","COPY",EDGE,{"derivedFrom":makeQuery(id+"F5.opBoolean","INTERSECT",EDGE,{"derivedFrom":[makeQuery(id+"F4.opPattern","COPY",FACE,{"derivedFrom":makeQuery(id+"F3.opExtrude","SWEPT_FACE",FACE,{"disambiguationData":[OSD([sQuery(id+"F2.wireOp",EDGE,"E6")])]}),"instanceName":"15"}),makeQuery(id+"F4.opPattern","COPY",FACE,{"derivedFrom":makeQuery(id+"F3.opExtrude","SWEPT_FACE",FACE,{"disambiguationData":[OSD([sQuery(id+"F2.wireOp",EDGE,"E7")])]}),"instanceName":"16"})]})});
            var Q49;
            Q49=makeQuery(id+"F6.opBoolean","COPY",EDGE,{"derivedFrom":makeQuery(id+"F4.opPattern","COPY",EDGE,{"derivedFrom":makeQuery(id+"F3.opExtrude","SWEPT_EDGE",EDGE,{"disambiguationData":[OSD([sQuery(id+"F2.wireOp",EDGE,"E6"),sQuery(id+"F2.wireOp",EDGE,"E7")])]}),"instanceName":"15"})});
            var Q50;
            Q50=makeQuery(id+"F6.opBoolean","COPY",EDGE,{"derivedFrom":makeQuery(id+"F5.opBoolean","INTERSECT",EDGE,{"derivedFrom":[makeQuery(id+"F4.opPattern","COPY",FACE,{"derivedFrom":makeQuery(id+"F3.opExtrude","SWEPT_FACE",FACE,{"disambiguationData":[OSD([sQuery(id+"F2.wireOp",EDGE,"E6")])]}),"instanceName":"13"}),makeQuery(id+"F4.opPattern","COPY",FACE,{"derivedFrom":makeQuery(id+"F3.opExtrude","SWEPT_FACE",FACE,{"disambiguationData":[OSD([sQuery(id+"F2.wireOp",EDGE,"E7")])]}),"instanceName":"14"})]})});
            var Q51;
            Q51=makeQuery(id+"F6.opBoolean","COPY",EDGE,{"derivedFrom":makeQuery(id+"F5.opBoolean","INTERSECT",EDGE,{"derivedFrom":[makeQuery(id+"F4.opPattern","COPY",FACE,{"derivedFrom":makeQuery(id+"F3.opExtrude","SWEPT_FACE",FACE,{"disambiguationData":[OSD([sQuery(id+"F2.wireOp",EDGE,"E6")])]}),"instanceName":"14"}),makeQuery(id+"F4.opPattern","COPY",FACE,{"derivedFrom":makeQuery(id+"F3.opExtrude","SWEPT_FACE",FACE,{"disambiguationData":[OSD([sQuery(id+"F2.wireOp",EDGE,"E7")])]}),"instanceName":"15"})]})});
            var Q52;
            Q52=makeQuery(id+"F6.opBoolean","COPY",EDGE,{"derivedFrom":makeQuery(id+"F4.opPattern","COPY",EDGE,{"derivedFrom":makeQuery(id+"F3.opExtrude","SWEPT_EDGE",EDGE,{"disambiguationData":[OSD([sQuery(id+"F2.wireOp",EDGE,"E6"),sQuery(id+"F2.wireOp",EDGE,"E7")])]}),"instanceName":"13"})});
            var Q53;
            Q53=makeQuery(id+"F6.opBoolean","COPY",EDGE,{"derivedFrom":makeQuery(id+"F5.opBoolean","INTERSECT",EDGE,{"derivedFrom":[makeQuery(id+"F4.opPattern","COPY",FACE,{"derivedFrom":makeQuery(id+"F3.opExtrude","SWEPT_FACE",FACE,{"disambiguationData":[OSD([sQuery(id+"F2.wireOp",EDGE,"E6")])]}),"instanceName":"12"}),makeQuery(id+"F4.opPattern","COPY",FACE,{"derivedFrom":makeQuery(id+"F3.opExtrude","SWEPT_FACE",FACE,{"disambiguationData":[OSD([sQuery(id+"F2.wireOp",EDGE,"E7")])]}),"instanceName":"13"})]})});
            var Q54;
            Q54=makeQuery(id+"F6.opBoolean","COPY",EDGE,{"derivedFrom":makeQuery(id+"F4.opPattern","COPY",EDGE,{"derivedFrom":makeQuery(id+"F3.opExtrude","SWEPT_EDGE",EDGE,{"disambiguationData":[OSD([sQuery(id+"F2.wireOp",EDGE,"E6"),sQuery(id+"F2.wireOp",EDGE,"E7")])]}),"instanceName":"12"})});
            var Q55;
            Q55=makeQuery(id+"F6.opBoolean","COPY",EDGE,{"derivedFrom":makeQuery(id+"F5.opBoolean","INTERSECT",EDGE,{"derivedFrom":[makeQuery(id+"F4.opPattern","COPY",FACE,{"derivedFrom":makeQuery(id+"F3.opExtrude","SWEPT_FACE",FACE,{"disambiguationData":[OSD([sQuery(id+"F2.wireOp",EDGE,"E6")])]}),"instanceName":"11"}),makeQuery(id+"F4.opPattern","COPY",FACE,{"derivedFrom":makeQuery(id+"F3.opExtrude","SWEPT_FACE",FACE,{"disambiguationData":[OSD([sQuery(id+"F2.wireOp",EDGE,"E7")])]}),"instanceName":"12"})]})});
            var Q56;
            Q56=makeQuery(id+"F6.opBoolean","COPY",EDGE,{"derivedFrom":makeQuery(id+"F4.opPattern","COPY",EDGE,{"derivedFrom":makeQuery(id+"F3.opExtrude","SWEPT_EDGE",EDGE,{"disambiguationData":[OSD([sQuery(id+"F2.wireOp",EDGE,"E6"),sQuery(id+"F2.wireOp",EDGE,"E7")])]}),"instanceName":"11"})});
            var Q57;
            Q57=makeQuery(id+"F6.opBoolean","COPY",EDGE,{"derivedFrom":makeQuery(id+"F5.opBoolean","INTERSECT",EDGE,{"derivedFrom":[makeQuery(id+"F4.opPattern","COPY",FACE,{"derivedFrom":makeQuery(id+"F3.opExtrude","SWEPT_FACE",FACE,{"disambiguationData":[OSD([sQuery(id+"F2.wireOp",EDGE,"E6")])]}),"instanceName":"10"}),makeQuery(id+"F4.opPattern","COPY",FACE,{"derivedFrom":makeQuery(id+"F3.opExtrude","SWEPT_FACE",FACE,{"disambiguationData":[OSD([sQuery(id+"F2.wireOp",EDGE,"E7")])]}),"instanceName":"11"})]})});
            var Q58;
            Q58=makeQuery(id+"F6.opBoolean","COPY",EDGE,{"derivedFrom":makeQuery(id+"F4.opPattern","COPY",EDGE,{"derivedFrom":makeQuery(id+"F3.opExtrude","SWEPT_EDGE",EDGE,{"disambiguationData":[OSD([sQuery(id+"F2.wireOp",EDGE,"E6"),sQuery(id+"F2.wireOp",EDGE,"E7")])]}),"instanceName":"10"})});
            var Q59;
            Q59=makeQuery(id+"F6.opBoolean","COPY",EDGE,{"derivedFrom":makeQuery(id+"F5.opBoolean","INTERSECT",EDGE,{"derivedFrom":[makeQuery(id+"F4.opPattern","COPY",FACE,{"derivedFrom":makeQuery(id+"F3.opExtrude","SWEPT_FACE",FACE,{"disambiguationData":[OSD([sQuery(id+"F2.wireOp",EDGE,"E6")])]}),"instanceName":"9"}),makeQuery(id+"F4.opPattern","COPY",FACE,{"derivedFrom":makeQuery(id+"F3.opExtrude","SWEPT_FACE",FACE,{"disambiguationData":[OSD([sQuery(id+"F2.wireOp",EDGE,"E7")])]}),"instanceName":"10"})]})});
            var Q60;
            Q60=makeQuery(id+"F6.opBoolean","COPY",EDGE,{"derivedFrom":makeQuery(id+"F4.opPattern","COPY",EDGE,{"derivedFrom":makeQuery(id+"F3.opExtrude","SWEPT_EDGE",EDGE,{"disambiguationData":[OSD([sQuery(id+"F2.wireOp",EDGE,"E6"),sQuery(id+"F2.wireOp",EDGE,"E7")])]}),"instanceName":"9"})});
            var Q61;
            Q61=makeQuery(id+"F6.opBoolean","COPY",EDGE,{"derivedFrom":makeQuery(id+"F5.opBoolean","INTERSECT",EDGE,{"derivedFrom":[makeQuery(id+"F4.opPattern","COPY",FACE,{"derivedFrom":makeQuery(id+"F3.opExtrude","SWEPT_FACE",FACE,{"disambiguationData":[OSD([sQuery(id+"F2.wireOp",EDGE,"E6")])]}),"instanceName":"8"}),makeQuery(id+"F4.opPattern","COPY",FACE,{"derivedFrom":makeQuery(id+"F3.opExtrude","SWEPT_FACE",FACE,{"disambiguationData":[OSD([sQuery(id+"F2.wireOp",EDGE,"E7")])]}),"instanceName":"9"})]})});
            var Q62;
            Q62=makeQuery(id+"F6.opBoolean","COPY",EDGE,{"derivedFrom":makeQuery(id+"F4.opPattern","COPY",EDGE,{"derivedFrom":makeQuery(id+"F3.opExtrude","SWEPT_EDGE",EDGE,{"disambiguationData":[OSD([sQuery(id+"F2.wireOp",EDGE,"E6"),sQuery(id+"F2.wireOp",EDGE,"E7")])]}),"instanceName":"8"})});
            var Q63;
            Q63=makeQuery(id+"F6.opBoolean","COPY",EDGE,{"derivedFrom":makeQuery(id+"F5.opBoolean","INTERSECT",EDGE,{"derivedFrom":[makeQuery(id+"F4.opPattern","COPY",FACE,{"derivedFrom":makeQuery(id+"F3.opExtrude","SWEPT_FACE",FACE,{"disambiguationData":[OSD([sQuery(id+"F2.wireOp",EDGE,"E6")])]}),"instanceName":"7"}),makeQuery(id+"F4.opPattern","COPY",FACE,{"derivedFrom":makeQuery(id+"F3.opExtrude","SWEPT_FACE",FACE,{"disambiguationData":[OSD([sQuery(id+"F2.wireOp",EDGE,"E7")])]}),"instanceName":"8"})]})});
            var Q64;
            Q64=makeQuery(id+"F6.opBoolean","COPY",EDGE,{"derivedFrom":makeQuery(id+"F4.opPattern","COPY",EDGE,{"derivedFrom":makeQuery(id+"F3.opExtrude","SWEPT_EDGE",EDGE,{"disambiguationData":[OSD([sQuery(id+"F2.wireOp",EDGE,"E6"),sQuery(id+"F2.wireOp",EDGE,"E7")])]}),"instanceName":"7"})});
            var Q65;
            Q65=makeQuery(id+"F6.opBoolean","COPY",EDGE,{"derivedFrom":makeQuery(id+"F5.opBoolean","INTERSECT",EDGE,{"derivedFrom":[makeQuery(id+"F4.opPattern","COPY",FACE,{"derivedFrom":makeQuery(id+"F3.opExtrude","SWEPT_FACE",FACE,{"disambiguationData":[OSD([sQuery(id+"F2.wireOp",EDGE,"E6")])]}),"instanceName":"6"}),makeQuery(id+"F4.opPattern","COPY",FACE,{"derivedFrom":makeQuery(id+"F3.opExtrude","SWEPT_FACE",FACE,{"disambiguationData":[OSD([sQuery(id+"F2.wireOp",EDGE,"E7")])]}),"instanceName":"7"})]})});
            fillet(context, id + "F7", {"entities" : qUnion([Q0, Q1, Q2, Q3, Q4, Q5, Q6, Q7, Q8, Q9, Q10, Q11, Q12, Q13, Q14, Q15, Q16, Q17, Q18, Q19, Q20, Q21, Q22, Q23, Q24, Q25, Q26, Q27, Q28, Q29, Q30, Q31, Q32, Q33, Q34, Q35, Q36, Q37, Q38, Q39, Q40, Q41, Q42, Q43, Q44, Q45, Q46, Q47, Q48, Q49, Q50, Q51, Q52, Q53, Q54, Q55, Q56, Q57, Q58, Q59, Q60, Q61, Q62, Q63, Q64, Q65]), "radius" : 0.4 * mm, "tangentPropagation" : true, "rho" : .3, "crossSection" : FilletCrossSection.CONIC, "allowEdgeOverflow" : false});
        }
    });
